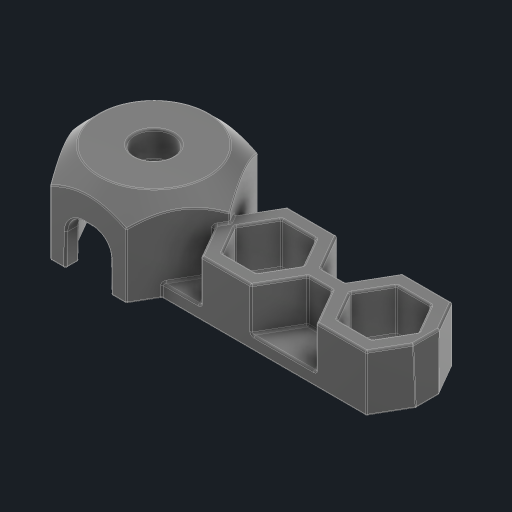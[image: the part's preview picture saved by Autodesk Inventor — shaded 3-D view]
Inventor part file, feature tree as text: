
AUTODESK INVENTOR PART (.ipt)
format: ipt  version: 2023 (Build 270158000, 158)  size: 638,464 bytes
history: native  units: in
note: dims shown in document units (in); Inventor stores cm internally (conversion verified against a paired STEP export)
features: fillet x1
ambient origin geometry x8: Origin, YZ Plane, XZ Plane, XY Plane, X Axis, Y Axis, Z Axis, Center Point
bodies: Solid1 (feature_tree)
feature tree (1):
  fillet  "Fillet23"  [1 undecoded]
note: 1 required parameter value undecoded (feature->parameter linkage not recoverable at this tier; creation-order binding heuristic only, values carry confidence <= 0.55)
